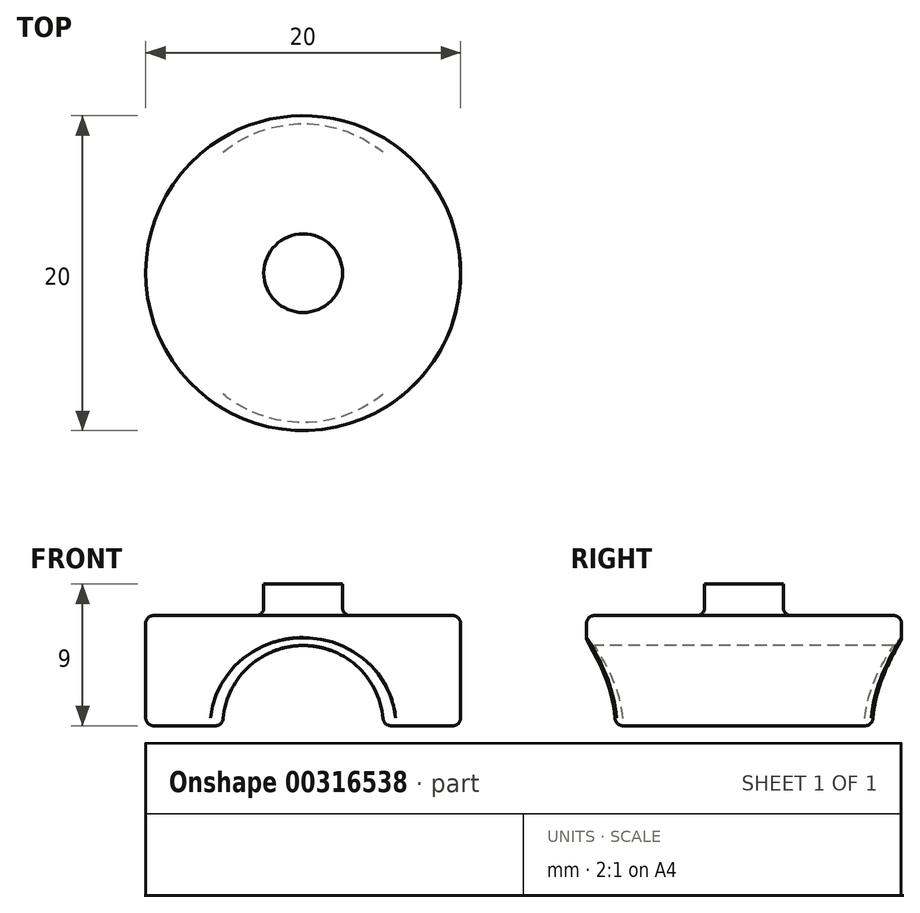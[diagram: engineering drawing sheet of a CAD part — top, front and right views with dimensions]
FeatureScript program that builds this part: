
annotation { "Feature Type Name" : "Feature", "Feature Type Description" : "" }
export const myFeature = defineFeature(function(context is Context, id is Id, definition is map)
    precondition{}
    {
        {
            var Q0;
            Q0=qCreatedBy(makeId("Top.planeOp"),FACE);
            var sketch = newSketch(context, id + "F0", { "sketchPlane" : qUnion([Q0])});
            skCircle(sketch, "E0", {"center": v(0, 0) * mm, "radius": 2.5 * mm});
            skSolve(sketch);
        }
        {
            var Q0;
            Q0 = qSketchRegion(id + "F0", true);
            extrude(context, id + "F1", {"entities" : qUnion([Q0]), "depth" : 9 * mm});
        }
        {
            var Q0;
            Q0=qCreatedBy(makeId("Top.planeOp"),FACE);
            var sketch = newSketch(context, id + "F2", { "sketchPlane" : qUnion([Q0])});
            skCircle(sketch, "E1", {"center": v(0, 0) * mm, "radius": 10 * mm});
            skSolve(sketch);
        }
        {
            var Q0;
            Q0=makeQuery(id+"F2.imprint","IMPRINT",FACE,{"disambiguationData":[TD([[makeQuery(id+"F2.imprint","IMPRINT",EDGE,{"derivedFrom":sQuery(id+"F2.wireOp",EDGE,"E1")}),1.0]])]});
            extrude(context, id + "F3", {"entities" : qUnion([Q0]), "operationType" : NewBodyOperationType.ADD, "depth" : 7 * mm});
        }
        {
            var Q0;
            Q0=qCreatedBy(makeId("Front.planeOp"),FACE);
            var sketch = newSketch(context, id + "F4", { "sketchPlane" : qUnion([Q0])});
            skCircle(sketch, "E2", {"center": v(0, 0) * mm, "radius": 5.1 * mm});
            skSolve(sketch);
        }
        {
            var Q0;
            Q0 = qSketchRegion(id + "F4", true);
            extrude(context, id + "F5", {"entities" : qUnion([Q0]), "operationType" : NewBodyOperationType.REMOVE, "oppositeDirection" : true, "depth" : 25 * mm, "hasSecondDirection" : true, "secondDirectionOppositeDirection" : false, "secondDirectionDepth" : 25 * mm});
        }
        {
            var Q0;
            Q0=makeQuery(id+"F3.opExtrude","CAP_EDGE",EDGE,{"disambiguationData":[OSD([sQuery(id+"F2.wireOp",EDGE,"E1")])],"isStart":false});
            fillet(context, id + "F6", {"entities" : qUnion([Q0]), "radius" : 0.5 * mm, "tangentPropagation" : true, "allowEdgeOverflow" : false});
        }
        {
            var Q0;
            Q0=makeQuery(id+"F5.boolean.opBoolean","SPLIT",EDGE,{"disambiguationData":[OD(1.0)],"derivedFrom":makeQuery(id+"F3.opExtrude","CAP_EDGE",EDGE,{"disambiguationData":[OSD([sQuery(id+"F2.wireOp",EDGE,"E1")])],"isStart":true})});
            var Q1;
            Q1=makeQuery(id+"F5.boolean.opBoolean","SPLIT",EDGE,{"disambiguationData":[OD(0.0)],"derivedFrom":makeQuery(id+"F3.opExtrude","CAP_EDGE",EDGE,{"disambiguationData":[OSD([sQuery(id+"F2.wireOp",EDGE,"E1")])],"isStart":true})});
            var Q2;
            Q2=makeQuery(id+"F5.boolean.opBoolean","INTERSECT",EDGE,{"disambiguationData":[OD(1.0)],"derivedFrom":[makeQuery(id+"F3.opExtrude","SWEPT_FACE",FACE,{"disambiguationData":[OSD([sQuery(id+"F2.wireOp",EDGE,"E1")])]}),makeQuery(id+"F5.opExtrude","SWEPT_FACE",FACE,{"disambiguationData":[OSD([sQuery(id+"F4.wireOp",EDGE,"E2")])]})]});
            var Q3;
            Q3=makeQuery(id+"F5.boolean.opBoolean","INTERSECT",EDGE,{"disambiguationData":[OD(0.0)],"derivedFrom":[makeQuery(id+"F3.opExtrude","SWEPT_FACE",FACE,{"disambiguationData":[OSD([sQuery(id+"F2.wireOp",EDGE,"E1")])]}),makeQuery(id+"F5.opExtrude","SWEPT_FACE",FACE,{"disambiguationData":[OSD([sQuery(id+"F4.wireOp",EDGE,"E2")])]})]});
            var Q4;
            Q4=makeQuery(id+"F5.boolean.opBoolean","INTERSECT",EDGE,{"disambiguationData":[OD(1.0)],"derivedFrom":[makeQuery(id+"F3.boolean.opBoolean","MERGE",FACE,{"derivedFrom":[makeQuery(id+"F1.opExtrude","CAP_FACE",FACE,{"disambiguationData":[OSD([sQuery(id+"F0.wireOp",EDGE,"E0")])],"isStart":true}),makeQuery(id+"F3.opExtrude","CAP_FACE",FACE,{"disambiguationData":[OSD([sQuery(id+"F2.wireOp",EDGE,"E1")])],"isStart":true})]}),makeQuery(id+"F5.opExtrude","SWEPT_FACE",FACE,{"disambiguationData":[OSD([sQuery(id+"F4.wireOp",EDGE,"E2")])]})]});
            var Q5;
            Q5=makeQuery(id+"F5.boolean.opBoolean","INTERSECT",EDGE,{"disambiguationData":[OD(0.0)],"derivedFrom":[makeQuery(id+"F3.boolean.opBoolean","MERGE",FACE,{"derivedFrom":[makeQuery(id+"F1.opExtrude","CAP_FACE",FACE,{"disambiguationData":[OSD([sQuery(id+"F0.wireOp",EDGE,"E0")])],"isStart":true}),makeQuery(id+"F3.opExtrude","CAP_FACE",FACE,{"disambiguationData":[OSD([sQuery(id+"F2.wireOp",EDGE,"E1")])],"isStart":true})]}),makeQuery(id+"F5.opExtrude","SWEPT_FACE",FACE,{"disambiguationData":[OSD([sQuery(id+"F4.wireOp",EDGE,"E2")])]})]});
            fillet(context, id + "F7", {"entities" : qUnion([Q0, Q1, Q2, Q3, Q4, Q5]), "radius" : 0.5 * mm, "tangentPropagation" : true, "allowEdgeOverflow" : false});
        }
        {
            var Q0;
            Q0=makeQuery(id+"F3.boolean.opBoolean","INTERSECT",EDGE,{"derivedFrom":[makeQuery(id+"F1.opExtrude","SWEPT_FACE",FACE,{"disambiguationData":[OSD([sQuery(id+"F0.wireOp",EDGE,"E0")])]}),makeQuery(id+"F3.opExtrude","CAP_FACE",FACE,{"disambiguationData":[OSD([sQuery(id+"F2.wireOp",EDGE,"E1")])],"isStart":false})]});
            fillet(context, id + "F8", {"entities" : qUnion([Q0]), "radius" : 0.5 * mm, "tangentPropagation" : true, "allowEdgeOverflow" : false});
        }
    });
